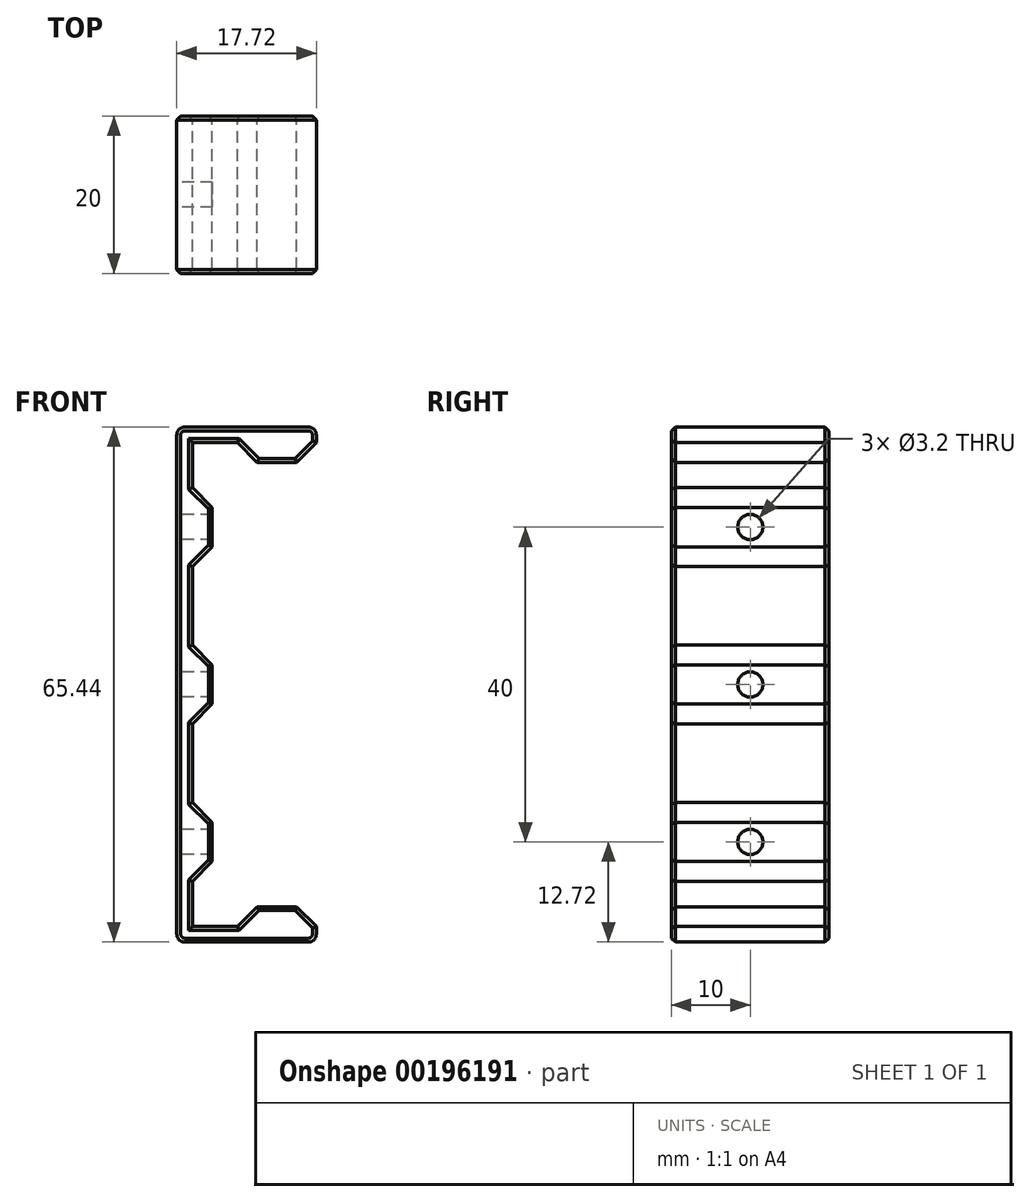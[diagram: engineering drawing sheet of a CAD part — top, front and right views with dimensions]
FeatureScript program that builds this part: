
annotation { "Feature Type Name" : "Feature", "Feature Type Description" : "" }
export const myFeature = defineFeature(function(context is Context, id is Id, definition is map)
    precondition{}
    {
        {
            var Q0;
            Q0=qCreatedBy(makeId("Front.planeOp"),FACE);
            var sketch = newSketch(context, id + "F0", { "sketchPlane" : qUnion([Q0])});
            skLineSegment(sketch, "E0", {"start": v(-5, 30.72) * mm, "end": v(5, 30.72) * mm, "construction": true});
            skLineSegment(sketch, "E1", {"start": v(-5, 30.72) * mm, "end": v(-2.5, 28.22) * mm});
            skLineSegment(sketch, "E2", {"start": v(5, 30.72) * mm, "end": v(2.5, 28.22) * mm});
            skLineSegment(sketch, "E3", {"start": v(-2.5, 28.22) * mm, "end": v(2.5, 28.22) * mm});
            skLineSegment(sketch, "E4", {"start": v(-4.58, 30.3) * mm, "end": v(4.58, 30.3) * mm, "construction": true});
            skPoint(sketch, "E5", {"position": v(0, 30.3) * mm});
            skLineSegment(sketch, "E6.MirrorCS", {"start": v(-2.5, -28.22) * mm, "end": v(2.5, -28.22) * mm});
            skLineSegment(sketch, "E7.MirrorCS", {"start": v(-5, -30.72) * mm, "end": v(-2.5, -28.22) * mm});
            skLineSegment(sketch, "E8.MirrorCS", {"start": v(5, -30.72) * mm, "end": v(2.5, -28.22) * mm});
            skLineSegment(sketch, "E9.bottom", {"start": v(-10.3, 30.3) * mm, "end": v(10.3, 30.3) * mm, "construction": true});
            skLineSegment(sketch, "E9.top", {"start": v(-10.3, -30.3) * mm, "end": v(10.3, -30.3) * mm, "construction": true});
            skLineSegment(sketch, "E9.left", {"start": v(-10.3, 30.3) * mm, "end": v(-10.3, -30.3) * mm, "construction": true});
            skLineSegment(sketch, "E9.right", {"start": v(10.3, 30.3) * mm, "end": v(10.3, -30.3) * mm, "construction": true});
            skPoint(sketch, "E10", {"position": v(-10.3, 0) * mm});
            skLineSegment(sketch, "E11", {"start": v(-8.22, 2.5) * mm, "end": v(-8.22, -2.5) * mm});
            skLineSegment(sketch, "E12", {"start": v(-10.72, 5) * mm, "end": v(-10.72, -5) * mm, "construction": true});
            skLineSegment(sketch, "E13", {"start": v(-10.72, 5) * mm, "end": v(-8.22, 2.5) * mm});
            skLineSegment(sketch, "E14", {"start": v(-10.72, -5) * mm, "end": v(-8.22, -2.5) * mm});
            skLineSegment(sketch, "E15", {"start": v(-10.3, 4.58) * mm, "end": v(-10.3, -4.58) * mm, "construction": true});
            skLineSegment(sketch, "E16", {"start": v(-20.57, 10) * mm, "end": v(32.03, 10) * mm, "construction": true});
            skLineSegment(sketch, "E17", {"start": v(-20.57, -10) * mm, "end": v(32.03, -10) * mm, "construction": true});
            skLineSegment(sketch, "E18.MirrorCS", {"start": v(-10.72, 15) * mm, "end": v(-8.22, 17.5) * mm});
            skLineSegment(sketch, "E19.MirrorCS", {"start": v(-8.22, 17.5) * mm, "end": v(-8.22, 22.5) * mm});
            skLineSegment(sketch, "E20.MirrorCS", {"start": v(-10.72, 25) * mm, "end": v(-8.22, 22.5) * mm});
            skLineSegment(sketch, "E21.MirrorCS", {"start": v(-10.72, -25) * mm, "end": v(-8.22, -22.5) * mm});
            skLineSegment(sketch, "E22.MirrorCS", {"start": v(-8.22, -22.5) * mm, "end": v(-8.22, -17.5) * mm});
            skLineSegment(sketch, "E23.MirrorCS", {"start": v(-10.72, -15) * mm, "end": v(-8.22, -17.5) * mm});
            skLineSegment(sketch, "E24", {"start": v(-10.72, -15) * mm, "end": v(-10.72, -5) * mm});
            skLineSegment(sketch, "E25", {"start": v(-10.72, 5) * mm, "end": v(-10.72, 15) * mm});
            skLineSegment(sketch, "E26", {"start": v(-10.72, -25) * mm, "end": v(-10.72, -30.72) * mm});
            skLineSegment(sketch, "E27", {"start": v(-10.72, -30.72) * mm, "end": v(-5, -30.72) * mm});
            skLineSegment(sketch, "E28", {"start": v(-10.72, 25) * mm, "end": v(-10.72, 30.72) * mm});
            skLineSegment(sketch, "E29", {"start": v(-10.72, 30.72) * mm, "end": v(-5, 30.72) * mm});
            skLineSegment(sketch, "E30", {"start": v(-12.72, 32.72) * mm, "end": v(-12.72, -32.72) * mm});
            skLineSegment(sketch, "E31", {"start": v(-12.72, 32.72) * mm, "end": v(5, 32.72) * mm});
            skLineSegment(sketch, "E32", {"start": v(-12.72, -32.72) * mm, "end": v(5, -32.72) * mm});
            skLineSegment(sketch, "E33", {"start": v(5, -30.72) * mm, "end": v(5, -32.72) * mm});
            skLineSegment(sketch, "E34", {"start": v(5, 30.72) * mm, "end": v(5, 32.72) * mm});
            skPoint(sketch, "E35", {"position": v(-8.22, 20) * mm});
            skPoint(sketch, "E36", {"position": v(-8.22, -20) * mm});
            skSolve(sketch);
        }
        {
            var Q0;
            Q0=makeQuery(id+"F0.imprint","IMPRINT",FACE,{"disambiguationData":[TD([[makeQuery(id+"F0.imprint","IMPRINT",EDGE,{"derivedFrom":sQuery(id+"F0.wireOp",EDGE,"E1")}),1.0]])]});
            extrude(context, id + "F1", {"entities" : qUnion([Q0]), "depth" : 20 * mm});
        }
        {
            var Q0;
            Q0=makeQuery(id+"F1.opExtrude","SWEPT_EDGE",EDGE,{"disambiguationData":[OSD([sQuery(id+"F0.wireOp",EDGE,"E31"),sQuery(id+"F0.wireOp",EDGE,"E34")])]});
            var Q1;
            Q1=makeQuery(id+"F1.opExtrude","SWEPT_EDGE",EDGE,{"disambiguationData":[OSD([sQuery(id+"F0.wireOp",EDGE,"E30"),sQuery(id+"F0.wireOp",EDGE,"E31")])]});
            var Q2;
            Q2=makeQuery(id+"F1.opExtrude","SWEPT_EDGE",EDGE,{"disambiguationData":[OSD([sQuery(id+"F0.wireOp",EDGE,"E30"),sQuery(id+"F0.wireOp",EDGE,"E32")])]});
            var Q3;
            Q3=makeQuery(id+"F1.opExtrude","SWEPT_EDGE",EDGE,{"disambiguationData":[OSD([sQuery(id+"F0.wireOp",EDGE,"E32"),sQuery(id+"F0.wireOp",EDGE,"E33")])]});
            fillet(context, id + "F2", {"entities" : qUnion([Q0, Q1, Q2, Q3]), "radius" : 1 * mm, "tangentPropagation" : true, "allowEdgeOverflow" : false});
        }
        {
            var Q0;
            Q0=makeQuery(id+"F1.opExtrude","SWEPT_FACE",FACE,{"disambiguationData":[OSD([sQuery(id+"F0.wireOp",EDGE,"E30")])]});
            var sketch = newSketch(context, id + "F3", { "sketchPlane" : qUnion([Q0])});
            skLineSegment(sketch, "E37.0", {"start": v(0, 17.5) * mm, "end": v(0, 22.5) * mm, "construction": true});
            skLineSegment(sketch, "E38.0", {"start": v(0, 2.5) * mm, "end": v(0, -2.5) * mm, "construction": true});
            skPoint(sketch, "E39", {"position": v(10, 20) * mm});
            skPoint(sketch, "E39.positionSnap0", {"position": v(0, 20) * mm});
            skPoint(sketch, "E39.positionSnap1", {"position": v(10, 31.72) * mm});
            skPoint(sketch, "E40", {"position": v(10, 0) * mm});
            skLineSegment(sketch, "E41.0", {"start": v(0, -22.5) * mm, "end": v(0, -17.5) * mm});
            skPoint(sketch, "E42", {"position": v(10, -20) * mm});
            skPoint(sketch, "E42.positionSnap0", {"position": v(0, -20) * mm});
            skSolve(sketch);
        }
        {
            var Q0;
            Q0=sQuery(id+"F3.wireOp",VERTEX,"E39");
            var Q1;
            Q1=sQuery(id+"F3.wireOp",VERTEX,"E40");
            var Q2;
            Q2=sQuery(id+"F3.wireOp",VERTEX,"E42");
            var Q3;
            Q3=makeQuery(id+"F1.opExtrude","SWEPT_BODY",BODY,{"disambiguationData":[OSD([sQuery(id+"F0.wireOp",EDGE,"E1"),sQuery(id+"F0.wireOp",EDGE,"E2"),sQuery(id+"F0.wireOp",EDGE,"E3"),sQuery(id+"F0.wireOp",EDGE,"E6.MirrorCS"),sQuery(id+"F0.wireOp",EDGE,"E7.MirrorCS"),sQuery(id+"F0.wireOp",EDGE,"E8.MirrorCS"),sQuery(id+"F0.wireOp",EDGE,"E11"),sQuery(id+"F0.wireOp",EDGE,"E13"),sQuery(id+"F0.wireOp",EDGE,"E14"),sQuery(id+"F0.wireOp",EDGE,"E18.MirrorCS"),sQuery(id+"F0.wireOp",EDGE,"E19.MirrorCS"),sQuery(id+"F0.wireOp",EDGE,"E20.MirrorCS"),sQuery(id+"F0.wireOp",EDGE,"E21.MirrorCS"),sQuery(id+"F0.wireOp",EDGE,"E22.MirrorCS"),sQuery(id+"F0.wireOp",EDGE,"E23.MirrorCS"),sQuery(id+"F0.wireOp",EDGE,"E24"),sQuery(id+"F0.wireOp",EDGE,"E25"),sQuery(id+"F0.wireOp",EDGE,"E26"),sQuery(id+"F0.wireOp",EDGE,"E27"),sQuery(id+"F0.wireOp",EDGE,"E28"),sQuery(id+"F0.wireOp",EDGE,"E29"),sQuery(id+"F0.wireOp",EDGE,"E30"),sQuery(id+"F0.wireOp",EDGE,"E31"),sQuery(id+"F0.wireOp",EDGE,"E32"),sQuery(id+"F0.wireOp",EDGE,"E33"),sQuery(id+"F0.wireOp",EDGE,"E34")])]});
            hole(context, id + "F4", {"style" : HoleStyle.SIMPLE, "endStyle" : HoleEndStyle.THROUGH, "holeDiameter" : 3.2 * mm, "locations" : qUnion([Q0, Q1, Q2]), "scope" : qUnion([Q3]), "isTappedThrough" : true});
        }
        {
            var Q0;
            Q0=makeQuery(id+"F1.opExtrude","CAP_FACE",FACE,{"disambiguationData":[OSD([sQuery(id+"F0.wireOp",EDGE,"E1"),sQuery(id+"F0.wireOp",EDGE,"E2"),sQuery(id+"F0.wireOp",EDGE,"E3"),sQuery(id+"F0.wireOp",EDGE,"E6.MirrorCS"),sQuery(id+"F0.wireOp",EDGE,"E7.MirrorCS"),sQuery(id+"F0.wireOp",EDGE,"E8.MirrorCS"),sQuery(id+"F0.wireOp",EDGE,"E11"),sQuery(id+"F0.wireOp",EDGE,"E13"),sQuery(id+"F0.wireOp",EDGE,"E14"),sQuery(id+"F0.wireOp",EDGE,"E18.MirrorCS"),sQuery(id+"F0.wireOp",EDGE,"E19.MirrorCS"),sQuery(id+"F0.wireOp",EDGE,"E20.MirrorCS"),sQuery(id+"F0.wireOp",EDGE,"E21.MirrorCS"),sQuery(id+"F0.wireOp",EDGE,"E22.MirrorCS"),sQuery(id+"F0.wireOp",EDGE,"E23.MirrorCS"),sQuery(id+"F0.wireOp",EDGE,"E24"),sQuery(id+"F0.wireOp",EDGE,"E25"),sQuery(id+"F0.wireOp",EDGE,"E26"),sQuery(id+"F0.wireOp",EDGE,"E27"),sQuery(id+"F0.wireOp",EDGE,"E28"),sQuery(id+"F0.wireOp",EDGE,"E29"),sQuery(id+"F0.wireOp",EDGE,"E30"),sQuery(id+"F0.wireOp",EDGE,"E31"),sQuery(id+"F0.wireOp",EDGE,"E32"),sQuery(id+"F0.wireOp",EDGE,"E33"),sQuery(id+"F0.wireOp",EDGE,"E34")])],"isStart":false});
            var Q1;
            Q1=makeQuery(id+"F1.opExtrude","CAP_FACE",FACE,{"disambiguationData":[OSD([sQuery(id+"F0.wireOp",EDGE,"E1"),sQuery(id+"F0.wireOp",EDGE,"E2"),sQuery(id+"F0.wireOp",EDGE,"E3"),sQuery(id+"F0.wireOp",EDGE,"E6.MirrorCS"),sQuery(id+"F0.wireOp",EDGE,"E7.MirrorCS"),sQuery(id+"F0.wireOp",EDGE,"E8.MirrorCS"),sQuery(id+"F0.wireOp",EDGE,"E11"),sQuery(id+"F0.wireOp",EDGE,"E13"),sQuery(id+"F0.wireOp",EDGE,"E14"),sQuery(id+"F0.wireOp",EDGE,"E18.MirrorCS"),sQuery(id+"F0.wireOp",EDGE,"E19.MirrorCS"),sQuery(id+"F0.wireOp",EDGE,"E20.MirrorCS"),sQuery(id+"F0.wireOp",EDGE,"E21.MirrorCS"),sQuery(id+"F0.wireOp",EDGE,"E22.MirrorCS"),sQuery(id+"F0.wireOp",EDGE,"E23.MirrorCS"),sQuery(id+"F0.wireOp",EDGE,"E24"),sQuery(id+"F0.wireOp",EDGE,"E25"),sQuery(id+"F0.wireOp",EDGE,"E26"),sQuery(id+"F0.wireOp",EDGE,"E27"),sQuery(id+"F0.wireOp",EDGE,"E28"),sQuery(id+"F0.wireOp",EDGE,"E29"),sQuery(id+"F0.wireOp",EDGE,"E30"),sQuery(id+"F0.wireOp",EDGE,"E31"),sQuery(id+"F0.wireOp",EDGE,"E32"),sQuery(id+"F0.wireOp",EDGE,"E33"),sQuery(id+"F0.wireOp",EDGE,"E34")])],"isStart":true});
            chamfer(context, id + "F5", {"entities" : qUnion([Q0, Q1]), "width" : 0.5 * mm, "tangentPropagation" : true});
        }
    });
